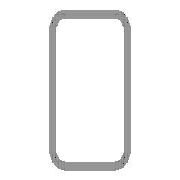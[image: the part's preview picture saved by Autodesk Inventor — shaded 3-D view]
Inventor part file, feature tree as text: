
AUTODESK INVENTOR PART (.ipt)
format: ipt  version: 2025.3 (Build 293356030, 356C)  size: 134,656 bytes
history: native  units: mm (DEFAULTED — no unit token found)
features: other x4, sketch x1, plane x1
ambient origin geometry x8: Origin, YZ Plane, XZ Plane, XY Plane, X Axis, Y Axis, Z Axis, Center Point
bodies: Solid1 (feature_tree), Body (feature_tree)
feature tree (6):
  parser-record x1  (decoder bookkeeping rows leaked as tree rows — omitted from the tree; the rows remain in map.json)
  other  "Driven Length"
  other  "Start Plane"
  other  "End Plane"
  sketch  "Sketch3"  dims[d3=190.0mm d4=0.0mm d7=4.0mm d9=20.0mm d11=40.0mm d12=2.0mm d13=40.0mm d14=230.0mm d15=10.0mm d16=20.0mm d17=90.0deg d18=190.0mm]
  plane  "Work Plane3"
